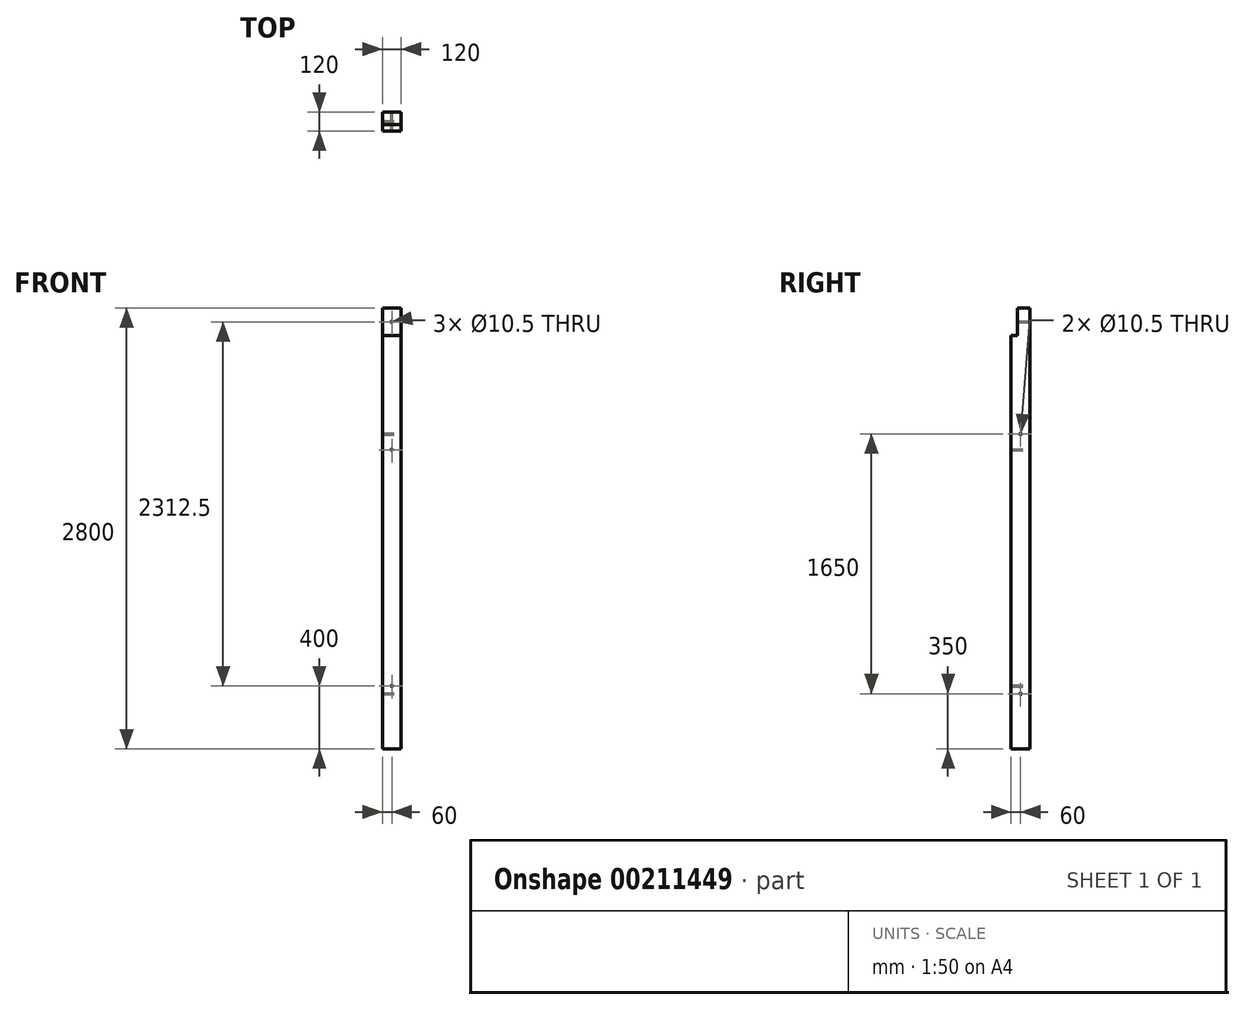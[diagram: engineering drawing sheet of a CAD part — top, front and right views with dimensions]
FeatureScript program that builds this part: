
annotation { "Feature Type Name" : "Feature", "Feature Type Description" : "" }
export const myFeature = defineFeature(function(context is Context, id is Id, definition is map)
    precondition{}
    {
        {
            var Q0;
            Q0=qCreatedBy(makeId("Top.planeOp"),FACE);
            var sketch = newSketch(context, id + "F0", { "sketchPlane" : qUnion([Q0])});
            skLineSegment(sketch, "E0", {"start": v(0, 0) * mm, "end": v(0, 330.83) * mm, "construction": true});
            skLineSegment(sketch, "E1", {"start": v(-296.67, 0) * mm, "end": v(360, 0) * mm, "construction": true});
            skLineSegment(sketch, "E2.bottom", {"start": v(60, 60) * mm, "end": v(-60, 60) * mm});
            skLineSegment(sketch, "E2.top", {"start": v(60, -60) * mm, "end": v(-60, -60) * mm});
            skLineSegment(sketch, "E2.left", {"start": v(60, 60) * mm, "end": v(60, -60) * mm});
            skLineSegment(sketch, "E2.right", {"start": v(-60, 60) * mm, "end": v(-60, -60) * mm});
            skPoint(sketch, "E2.middle", {"position": v(0, 0) * mm});
            skPoint(sketch, "E3.visualSharp", {"position": v(-60, 60) * mm});
            skPoint(sketch, "E4.visualSharp", {"position": v(60, 60) * mm});
            skPoint(sketch, "E5.visualSharp", {"position": v(-60, -60) * mm});
            skPoint(sketch, "E6.visualSharp", {"position": v(60, -60) * mm});
            skSolve(sketch);
        }
        {
            var Q0;
            Q0=qSketchRegion(id+"F0",true);
            extrude(context, id + "F1", {"entities" : qUnion([Q0]), "depth" : 2800 * mm, "symmetric" : true});
        }
        {
            var Q0;
            Q0=makeQuery(id+"F1.opExtrude","SWEPT_FACE",FACE,{"disambiguationData":[OSD([sQuery(id+"F0.wireOp",EDGE,"E2.left")])]});
            var sketch = newSketch(context, id + "F2", { "sketchPlane" : qUnion([Q0])});
            skLineSegment(sketch, "E7.bottom", {"start": v(-60, 1400) * mm, "end": v(-20, 1400) * mm});
            skLineSegment(sketch, "E7.top", {"start": v(-60, 1225) * mm, "end": v(-20, 1225) * mm});
            skLineSegment(sketch, "E7.left", {"start": v(-60, 1400) * mm, "end": v(-60, 1225) * mm});
            skLineSegment(sketch, "E7.right", {"start": v(-20, 1400) * mm, "end": v(-20, 1225) * mm});
            skSolve(sketch);
        }
        {
            var Q0;
            Q0=qSketchRegion(id+"F2",true);
            extrude(context, id + "F3", {"entities" : qUnion([Q0]), "operationType" : NewBodyOperationType.REMOVE, "endBound" : BoundingType.UP_TO_NEXT, "oppositeDirection" : true, "depth" : 25 * mm});
        }
        {
            var Q0;
            Q0=makeQuery(id+"F1.opExtrude","SWEPT_FACE",FACE,{"disambiguationData":[OSD([sQuery(id+"F0.wireOp",EDGE,"E2.bottom")])]});
            var sketch = newSketch(context, id + "F4", { "sketchPlane" : qUnion([Q0])});
            skCircle(sketch, "E8", {"center": v(0, 1312.5) * mm, "radius": 5.25 * mm});
            skCircle(sketch, "E9", {"center": v(0, -1000) * mm, "radius": 5.25 * mm});
            skCircle(sketch, "E10", {"center": v(0, 500) * mm, "radius": 5.25 * mm});
            skSolve(sketch);
        }
        {
            var Q0;
            Q0=qSketchRegion(id+"F4",true);
            extrude(context, id + "F5", {"entities" : qUnion([Q0]), "operationType" : NewBodyOperationType.REMOVE, "endBound" : BoundingType.THROUGH_ALL, "oppositeDirection" : true, "depth" : 25 * mm});
        }
        {
            var Q0;
            Q0=makeQuery(id+"F1.opExtrude","SWEPT_FACE",FACE,{"disambiguationData":[OSD([sQuery(id+"F0.wireOp",EDGE,"E2.left")])]});
            var sketch = newSketch(context, id + "F6", { "sketchPlane" : qUnion([Q0])});
            skCircle(sketch, "E11", {"center": v(0, -1050) * mm, "radius": 5.25 * mm});
            skCircle(sketch, "E12", {"center": v(0, 600) * mm, "radius": 5.25 * mm});
            skSolve(sketch);
        }
        {
            var Q0;
            Q0=qSketchRegion(id+"F6",true);
            extrude(context, id + "F7", {"entities" : qUnion([Q0]), "operationType" : NewBodyOperationType.REMOVE, "endBound" : BoundingType.THROUGH_ALL, "oppositeDirection" : true, "depth" : 25 * mm});
        }
    });
